# Revit family: Electronics_Visual-TVs_ViewSonic_ViewSonicR-CDE6520-7520-8620-commercial-display
name_source: partatom
category: Electrical Equipment
revit_build: Autodesk Revit 2017 (Build: 20190508_0315(x64)
units: mm (PartAtom-declared; Revit-internal decimal feet)

## family parameters
Always vertical = Yes
Cut with Voids When Loaded = No
OmniClass Number = 23.85.10.14.24.17
OmniClass Title = Plasma Video Monitors
Panel Configuration = Two Columns, Circuits Across
Part Type = Panelboard
Room Calculation Point = No
Round Connector Dimension = Use Diameter
Shared = No
Work Plane-Based = No

## types (3) — shared parameters
Aspect Ratio = 16:9
Assembly Code = D5030500
Backlight = WLED
Backlight Life = 30,000 Hours (min)
Bezel = Slim
Brightness = 450 nits (typ.)
Colors = 1.07G colors
Contrast Ratio = 1200:1 Typ.
Cover Material = Plastic - ViewSonic - Black
Covering Color = Plastic - ViewSonic - Black
Edition number = 1
Hardness = 3H
Keynote = 11130
Light Source = DLED
Manufacturer = ViewSonic
Native Resolution = 3840 x 2160
Orientation = Landscape
Product data url = https://www.bimobject.com
Response Time = 8 ms
Surface Treatment = Anti-glare, 3H hardness, Haze 25%
Type/ Tech = TFT LCD Module. IPS type, DLED backlight
URL = https://www.viewsonic.com
Viewing Angles = H = 178, V = 178 typ.

## per-type parameters (varying)
| type | CDE6520 | CDE7520 | CDE8620 | Description | Display Area (mm) | Display Size | Model | Panel Size | Product Guid | Resolution | Screen Material | Viewable Area (In.) |
| CDE 6520 | Yes | No | No | The ViewSonic® CDE6520 is a 65” premium 4K commercial display. With features including a razor-sharp resolution of 3840 x 2160, 450-nit high brightness, 178-degree ultra- wide viewing angles, 2 x 12W speakers, and wireless screen sharing, the display is designed with the meeting room scenario in mind. The built-in screen sharing software*, ViewBoard® Cast and Stream, as well as ViewBoard® Cast USB-C sender enable multiple users, whether on-site or on-line, to participate in conferences and share content with each other simultaneously, transforming the CDE6520 into a dynamic content hub. This reliable commercial display is equipped with a quad-core processor and 16GB internal memory, allowing constant multimedia play from internal storage or a USB flash drive. Supporting remote configuration and content management system, the ViewSonic® CDE6520 is also suitable for diverse signage applications. *Chrome, Android, Windows, Mac OS, and iOS complaint | 1428.48(H) × 803.52(V) (65" diagonal) | 65" | viewsonic_cde6520 | 65" | cf630bab-5e48-463c-9237-2bb45ea75d06 | 3840x2160; 16:9 | Screen - ViewSonic - CDE6520 | 65" |
| CDE 7520 | No | Yes | No | The ViewSonic® CDE7520 is a 75” premium 4K commercial display. With features including a razor-sharp resolution of 3840 x 2160, 450-nit high brightness, 178-degree ultra- wide viewing angles, 2 x 12W speakers, and wireless screen sharing, the display is designed with the meeting room scenario in mind. The built-in screen sharing software*, ViewBoard® Cast and Stream, as well as ViewBoard® Cast USB-C sender enable multiple users, whether on-site or on-line, to participate in conferences and share content with each other simultaneously, transforming the CDE7520 into a dynamic content hub. This reliable commercial display is equipped with a quad-core processor and 16GB internal memory, allowing constant multimedia play from internal storage or a USB flash drive. Supporting remote configuration and content management system, the ViewSonic® CDE7520 is also suitable for diverse signage applications. *Chrome, Android, Windows, Mac OS, and iOS complaint | 1649.664(H) × 927.936(V) (75" diagonal) | 75" | viewsonic_cde7520 | 75" | 9c57ebf9-71ef-4f29-a4d3-039314f2a187 | 3840 x 2160; 16:9 | Screen - ViewSonic - CDE7520 | 75" |
| CDE 8620 | No | No | Yes | The ViewSonic® CDE8620 is a 86” premium 4K commercial display. With features including a razor-sharp resolution of 3840 x 2160, 450-nit high brightness, 178-degree ultra- wide viewing angles, 2 x 12W speakers, and wireless screen sharing, the display is designed with the meeting room scenario in mind. The built-in screen sharing software*, ViewBoard® Cast and Stream, as well as ViewBoard® Cast USB-C sender enable multiple users, whether on-site or on-line, to participate in conferences and share content with each other simultaneously, transforming the CDE8620 into a dynamic content hub. This reliable commercial display is equipped with a quad-core processor and 16GB internal memory, allowing constant multimedia play from internal storage or a USB flash drive. Supporting remote configuration and content management system, the ViewSonic® CDE8620 is also suitable for diverse signage applications. *Chrome, Android, Windows, Mac OS, and iOS complaint | 1895.040 (H) × 1065.960 (V) (86" diagonal) | 86" | viewsonic_cde8620 | 86" | c44e1a28-d053-46cf-849a-4aad2d66661b | 3840 x 2160; 16:9 | Screen - ViewSonic - CDE8620 | 86" |

## geometry (parser evidence)
native form markers: Sweep x9
no freeform markers — native parametric forms only
